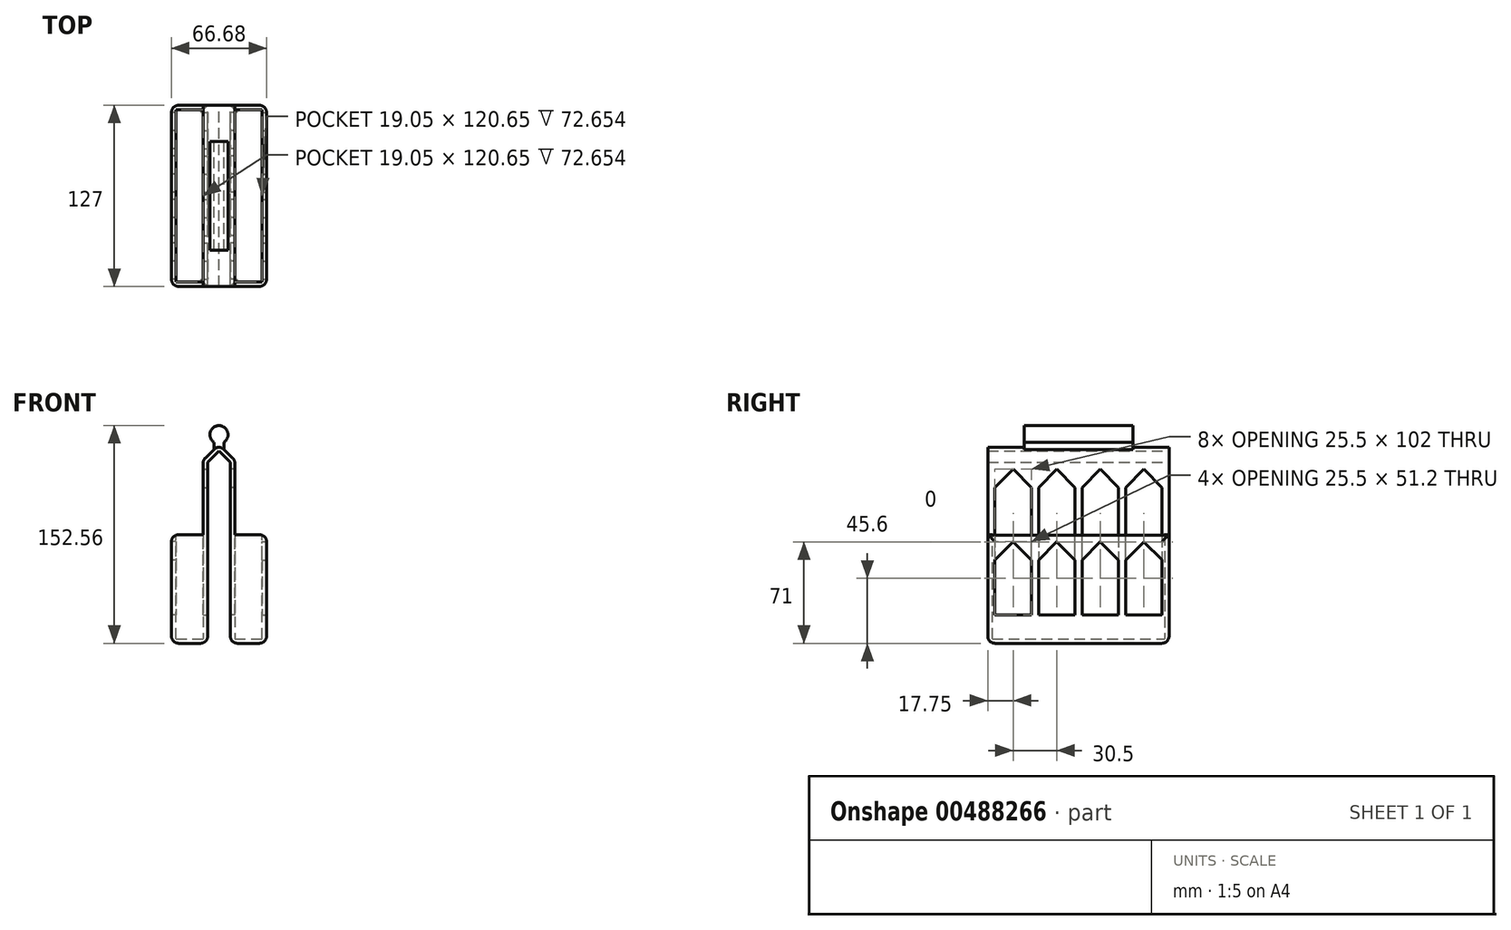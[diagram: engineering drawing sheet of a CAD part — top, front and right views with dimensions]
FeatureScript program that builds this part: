
annotation { "Feature Type Name" : "Feature", "Feature Type Description" : "" }
export const myFeature = defineFeature(function(context is Context, id is Id, definition is map)
    precondition{}
    {
        {
            var Q0;
            Q0=qCreatedBy(makeId("Front.planeOp"),FACE);
            var sketch = newSketch(context, id + "F0", { "sketchPlane" : qUnion([Q0])});
            skLineSegment(sketch, "E0.MirrorCS", {"start": v(7.94, 45.45) * mm, "end": v(0, 53.39) * mm});
            skLineSegment(sketch, "E1.MirrorCS", {"start": v(7.94, 45.45) * mm, "end": v(7.94, -81.55) * mm});
            skLineSegment(sketch, "E2.MirrorCS", {"start": v(7.94, -81.55) * mm, "end": v(33.34, -81.55) * mm});
            skLineSegment(sketch, "E3.MirrorCS", {"start": v(33.34, -81.55) * mm, "end": v(33.34, -5.35) * mm});
            skLineSegment(sketch, "E4.4", {"start": v(30.16, -78.37) * mm, "end": v(30.16, -5.35) * mm});
            skLineSegment(sketch, "E4.5", {"start": v(11.11, -78.37) * mm, "end": v(30.16, -78.37) * mm});
            skLineSegment(sketch, "E4.6", {"start": v(11.11, 46.77) * mm, "end": v(11.11, -78.37) * mm});
            skLineSegment(sketch, "E4.7", {"start": v(11.11, 46.77) * mm, "end": v(0, 57.88) * mm});
            skLineSegment(sketch, "E5", {"start": v(30.16, -5.35) * mm, "end": v(33.34, -5.35) * mm});
            skLineSegment(sketch, "E6", {"start": v(0, 57.88) * mm, "end": v(0, 53.39) * mm});
            skSolve(sketch);
        }
        {
            var Q0;
            Q0=makeQuery(id+"F0.imprint","IMPRINT",FACE,{"disambiguationData":[TD([[makeQuery(id+"F0.imprint","IMPRINT",EDGE,{"derivedFrom":sQuery(id+"F0.wireOp",EDGE,"E0.MirrorCS")}),-1.0]])]});
            extrude(context, id + "F1", {"entities" : qUnion([Q0]), "depth" : 127 * mm, "symmetric" : true});
        }
        {
            var Q0;
            Q0=makeQuery(id+"F1.opExtrude","SWEPT_FACE",FACE,{"disambiguationData":[OSD([sQuery(id+"F0.wireOp",EDGE,"E3.MirrorCS")])]});
            var sketch = newSketch(context, id + "F2", { "sketchPlane" : qUnion([Q0])});
            skLineSegment(sketch, "E7", {"start": v(-58.5, -23.1) * mm, "end": v(-58.5, -61.55) * mm});
            skLineSegment(sketch, "E8", {"start": v(-58.5, -61.55) * mm, "end": v(-33, -61.55) * mm});
            skLineSegment(sketch, "E9", {"start": v(-33, -61.55) * mm, "end": v(-33, -23.1) * mm});
            skLineSegment(sketch, "E10", {"start": v(-33, -23.1) * mm, "end": v(-45.75, -10.35) * mm});
            skLineSegment(sketch, "E11", {"start": v(-45.75, -10.35) * mm, "end": v(-58.5, -23.1) * mm});
            skLineSegment(sketch, "E12", {"start": v(-28, -61.55) * mm, "end": v(-2.5, -61.55) * mm});
            skLineSegment(sketch, "E13", {"start": v(-2.5, -61.55) * mm, "end": v(-2.5, -23.1) * mm});
            skLineSegment(sketch, "E14", {"start": v(-2.5, -23.1) * mm, "end": v(-15.25, -10.35) * mm});
            skLineSegment(sketch, "E15", {"start": v(-15.25, -10.35) * mm, "end": v(-28, -23.1) * mm});
            skLineSegment(sketch, "E16", {"start": v(-28, -23.1) * mm, "end": v(-28, -61.55) * mm});
            skLineSegment(sketch, "E17.MirrorCS", {"start": v(58.5, -61.55) * mm, "end": v(33, -61.55) * mm});
            skLineSegment(sketch, "E18.MirrorCS", {"start": v(45.75, -10.35) * mm, "end": v(58.5, -23.1) * mm});
            skLineSegment(sketch, "E19.MirrorCS", {"start": v(2.5, -61.55) * mm, "end": v(2.5, -23.1) * mm});
            skLineSegment(sketch, "E20.MirrorCS", {"start": v(28, -61.55) * mm, "end": v(2.5, -61.55) * mm});
            skLineSegment(sketch, "E21.MirrorCS", {"start": v(33, -61.55) * mm, "end": v(33, -23.1) * mm});
            skLineSegment(sketch, "E22.MirrorCS", {"start": v(15.25, -10.35) * mm, "end": v(28, -23.1) * mm});
            skLineSegment(sketch, "E23.MirrorCS", {"start": v(58.5, -23.1) * mm, "end": v(58.5, -61.55) * mm});
            skLineSegment(sketch, "E24.MirrorCS", {"start": v(28, -23.1) * mm, "end": v(28, -61.55) * mm});
            skLineSegment(sketch, "E25.MirrorCS", {"start": v(33, -23.1) * mm, "end": v(45.75, -10.35) * mm});
            skLineSegment(sketch, "E26.MirrorCS", {"start": v(2.5, -23.1) * mm, "end": v(15.25, -10.35) * mm});
            skSolve(sketch);
        }
        {
            var Q0;
            Q0=makeQuery(id+"F2.imprint","IMPRINT",FACE,{"disambiguationData":[TD([[makeQuery(id+"F2.imprint","IMPRINT",EDGE,{"derivedFrom":sQuery(id+"F2.wireOp",EDGE,"E7")}),1.0]])]});
            var Q1;
            Q1=makeQuery(id+"F2.imprint","IMPRINT",FACE,{"disambiguationData":[TD([[makeQuery(id+"F2.imprint","IMPRINT",EDGE,{"derivedFrom":sQuery(id+"F2.wireOp",EDGE,"E12")}),1.0]])]});
            var Q2;
            Q2=makeQuery(id+"F2.imprint","IMPRINT",FACE,{"disambiguationData":[TD([[makeQuery(id+"F2.imprint","IMPRINT",EDGE,{"derivedFrom":sQuery(id+"F2.wireOp",EDGE,"E19.MirrorCS")}),-1.0]])]});
            var Q3;
            Q3=makeQuery(id+"F2.imprint","IMPRINT",FACE,{"disambiguationData":[TD([[makeQuery(id+"F2.imprint","IMPRINT",EDGE,{"derivedFrom":sQuery(id+"F2.wireOp",EDGE,"E17.MirrorCS")}),-1.0]])]});
            extrude(context, id + "F3", {"entities" : qUnion([Q0, Q1, Q2, Q3]), "operationType" : NewBodyOperationType.REMOVE, "endBound" : BoundingType.UP_TO_NEXT, "oppositeDirection" : true, "depth" : 25.4 * mm});
        }
        {
            var Q0;
            Q0=makeQuery(id+"F1.opExtrude","SWEPT_FACE",FACE,{"disambiguationData":[OSD([sQuery(id+"F0.wireOp",EDGE,"E1.MirrorCS")])]});
            var sketch = newSketch(context, id + "F4", { "sketchPlane" : qUnion([Q0])});
            skLineSegment(sketch, "E27", {"start": v(-58.5, 27.7) * mm, "end": v(-58.5, -61.55) * mm});
            skLineSegment(sketch, "E28", {"start": v(-58.5, -61.55) * mm, "end": v(-33, -61.55) * mm});
            skLineSegment(sketch, "E29", {"start": v(-33, -61.55) * mm, "end": v(-33, 27.7) * mm});
            skLineSegment(sketch, "E30", {"start": v(-33, 27.7) * mm, "end": v(-45.75, 40.45) * mm});
            skLineSegment(sketch, "E31", {"start": v(-45.75, 40.45) * mm, "end": v(-58.5, 27.7) * mm});
            skLineSegment(sketch, "E32", {"start": v(-28, -61.55) * mm, "end": v(-2.5, -61.55) * mm});
            skLineSegment(sketch, "E33", {"start": v(-2.5, -61.55) * mm, "end": v(-2.5, 27.7) * mm});
            skLineSegment(sketch, "E34", {"start": v(-2.5, 27.7) * mm, "end": v(-15.25, 40.45) * mm});
            skLineSegment(sketch, "E35", {"start": v(-15.25, 40.45) * mm, "end": v(-28, 27.7) * mm});
            skLineSegment(sketch, "E36", {"start": v(-28, 27.7) * mm, "end": v(-28, -61.55) * mm});
            skLineSegment(sketch, "E37.MirrorCS", {"start": v(58.5, 27.7) * mm, "end": v(58.5, -61.55) * mm});
            skLineSegment(sketch, "E38.MirrorCS", {"start": v(58.5, -61.55) * mm, "end": v(33, -61.55) * mm});
            skLineSegment(sketch, "E39.MirrorCS", {"start": v(33, -61.55) * mm, "end": v(33, 27.7) * mm});
            skLineSegment(sketch, "E40.MirrorCS", {"start": v(33, 27.7) * mm, "end": v(45.75, 40.45) * mm});
            skLineSegment(sketch, "E41.MirrorCS", {"start": v(28, 27.7) * mm, "end": v(28, -61.55) * mm});
            skLineSegment(sketch, "E42.MirrorCS", {"start": v(45.75, 40.45) * mm, "end": v(58.5, 27.7) * mm});
            skLineSegment(sketch, "E43.MirrorCS", {"start": v(28, -61.55) * mm, "end": v(2.5, -61.55) * mm});
            skLineSegment(sketch, "E44.MirrorCS", {"start": v(15.25, 40.45) * mm, "end": v(28, 27.7) * mm});
            skLineSegment(sketch, "E45.MirrorCS", {"start": v(2.5, -61.55) * mm, "end": v(2.5, 27.7) * mm});
            skLineSegment(sketch, "E46.MirrorCS", {"start": v(2.5, 27.7) * mm, "end": v(15.25, 40.45) * mm});
            skSolve(sketch);
        }
        {
            var Q0;
            Q0=makeQuery(id+"F4.imprint","IMPRINT",FACE,{"disambiguationData":[TD([[makeQuery(id+"F4.imprint","IMPRINT",EDGE,{"derivedFrom":sQuery(id+"F4.wireOp",EDGE,"E27")}),1.0]])]});
            var Q1;
            Q1=makeQuery(id+"F4.imprint","IMPRINT",FACE,{"disambiguationData":[TD([[makeQuery(id+"F4.imprint","IMPRINT",EDGE,{"derivedFrom":sQuery(id+"F4.wireOp",EDGE,"E32")}),1.0]])]});
            var Q2;
            Q2=makeQuery(id+"F4.imprint","IMPRINT",FACE,{"disambiguationData":[TD([[makeQuery(id+"F4.imprint","IMPRINT",EDGE,{"derivedFrom":sQuery(id+"F4.wireOp",EDGE,"E41.MirrorCS")}),-1.0]])]});
            var Q3;
            Q3=makeQuery(id+"F4.imprint","IMPRINT",FACE,{"disambiguationData":[TD([[makeQuery(id+"F4.imprint","IMPRINT",EDGE,{"derivedFrom":sQuery(id+"F4.wireOp",EDGE,"E37.MirrorCS")}),-1.0]])]});
            extrude(context, id + "F5", {"entities" : qUnion([Q0, Q1, Q2, Q3]), "operationType" : NewBodyOperationType.REMOVE, "endBound" : BoundingType.UP_TO_NEXT, "oppositeDirection" : true, "depth" : 25.4 * mm});
        }
        {
            var Q0;
            Q0=makeQuery(id+"F1.opExtrude","SWEPT_BODY",BODY,{"disambiguationData":[OSD([sQuery(id+"F0.wireOp",EDGE,"E0.MirrorCS"),sQuery(id+"F0.wireOp",EDGE,"E1.MirrorCS"),sQuery(id+"F0.wireOp",EDGE,"E2.MirrorCS"),sQuery(id+"F0.wireOp",EDGE,"E3.MirrorCS"),sQuery(id+"F0.wireOp",EDGE,"E4.4"),sQuery(id+"F0.wireOp",EDGE,"E4.5"),sQuery(id+"F0.wireOp",EDGE,"E4.6"),sQuery(id+"F0.wireOp",EDGE,"E4.7"),sQuery(id+"F0.wireOp",EDGE,"E5"),sQuery(id+"F0.wireOp",EDGE,"E6")])]});
            var Q1;
            Q1=qCreatedBy(makeId("Right.planeOp"),FACE);
            mirror(context, id + "F6", {"operationType" : NewBodyOperationType.ADD, "entities" : qUnion([Q0]), "mirrorPlane" : qUnion([Q1])});
        }
        {
            var Q0;
            {var subQ0=makeQuery(id+"F1.opExtrude","CAP_FACE",FACE,{"disambiguationData":[OSD([sQuery(id+"F0.wireOp",EDGE,"E0.MirrorCS"),sQuery(id+"F0.wireOp",EDGE,"E1.MirrorCS"),sQuery(id+"F0.wireOp",EDGE,"E2.MirrorCS"),sQuery(id+"F0.wireOp",EDGE,"E3.MirrorCS"),sQuery(id+"F0.wireOp",EDGE,"E4.4"),sQuery(id+"F0.wireOp",EDGE,"E4.5"),sQuery(id+"F0.wireOp",EDGE,"E4.6"),sQuery(id+"F0.wireOp",EDGE,"E4.7"),sQuery(id+"F0.wireOp",EDGE,"E5"),sQuery(id+"F0.wireOp",EDGE,"E6")])],"isStart":true});Q0=makeQuery(id+"F6.boolean.opBoolean","MERGE",FACE,{"derivedFrom":[subQ0,makeQuery(id+"F6.opPattern","COPY",FACE,{"derivedFrom":subQ0,"instanceName":"1"})]});}
            var sketch = newSketch(context, id + "F7", { "sketchPlane" : qUnion([Q0])});
            skLineSegment(sketch, "E47.bottom", {"start": v(-33.34, -5.35) * mm, "end": v(-7.94, -5.35) * mm});
            skLineSegment(sketch, "E47.top", {"start": v(-33.34, -81.55) * mm, "end": v(-7.94, -81.55) * mm});
            skLineSegment(sketch, "E47.left", {"start": v(-33.34, -5.35) * mm, "end": v(-33.34, -81.55) * mm});
            skLineSegment(sketch, "E47.right", {"start": v(-7.94, -5.35) * mm, "end": v(-7.94, -81.55) * mm});
            skLineSegment(sketch, "E48.bottom", {"start": v(33.34, -5.35) * mm, "end": v(7.94, -5.35) * mm});
            skLineSegment(sketch, "E48.top", {"start": v(33.34, -81.55) * mm, "end": v(7.94, -81.55) * mm});
            skLineSegment(sketch, "E48.left", {"start": v(33.34, -5.35) * mm, "end": v(33.34, -81.55) * mm});
            skLineSegment(sketch, "E48.right", {"start": v(7.94, -5.35) * mm, "end": v(7.94, -81.55) * mm});
            skSolve(sketch);
        }
        {
            var Q0;
            {var subQ1=makeQuery(id+"F1.opExtrude","CAP_EDGE",EDGE,{"disambiguationData":[OSD([sQuery(id+"F0.wireOp",EDGE,"E4.4")])],"isStart":true});Q0=makeQuery(id+"F7.imprint","IMPRINT",FACE,{"disambiguationData":[TD([[makeQuery(id+"F7.imprint","IMPRINT",EDGE,{"derivedFrom":subQ1}),-1.0]])]});}
            var Q1;
            Q1=makeQuery(id+"F7.imprint","IMPRINT",FACE,{"disambiguationData":[TD([[makeQuery(id+"F7.imprint","IMPRINT",EDGE,{"derivedFrom":sQuery(id+"F7.wireOp",EDGE,"E47.top")}),-1.0]])]});
            var Q2;
            {var subQ1=makeQuery(id+"F6.opPattern","COPY",EDGE,{"derivedFrom":makeQuery(id+"F1.opExtrude","CAP_EDGE",EDGE,{"disambiguationData":[OSD([sQuery(id+"F0.wireOp",EDGE,"E4.4")])],"isStart":true}),"instanceName":"1"});Q2=makeQuery(id+"F7.imprint","IMPRINT",FACE,{"disambiguationData":[TD([[makeQuery(id+"F7.imprint","IMPRINT",EDGE,{"derivedFrom":subQ1}),1.0]])]});}
            var Q3;
            Q3=makeQuery(id+"F7.imprint","IMPRINT",FACE,{"disambiguationData":[TD([[makeQuery(id+"F7.imprint","IMPRINT",EDGE,{"derivedFrom":sQuery(id+"F7.wireOp",EDGE,"E48.top")}),1.0]])]});
            extrude(context, id + "F8", {"entities" : qUnion([Q0, Q1, Q2, Q3]), "operationType" : NewBodyOperationType.ADD, "oppositeDirection" : true, "depth" : 3.17 * mm});
        }
        {
            var Q0;
            {var subQ0=makeQuery(id+"F1.opExtrude","CAP_FACE",FACE,{"disambiguationData":[OSD([sQuery(id+"F0.wireOp",EDGE,"E0.MirrorCS"),sQuery(id+"F0.wireOp",EDGE,"E1.MirrorCS"),sQuery(id+"F0.wireOp",EDGE,"E2.MirrorCS"),sQuery(id+"F0.wireOp",EDGE,"E3.MirrorCS"),sQuery(id+"F0.wireOp",EDGE,"E4.4"),sQuery(id+"F0.wireOp",EDGE,"E4.5"),sQuery(id+"F0.wireOp",EDGE,"E4.6"),sQuery(id+"F0.wireOp",EDGE,"E4.7"),sQuery(id+"F0.wireOp",EDGE,"E5"),sQuery(id+"F0.wireOp",EDGE,"E6")])],"isStart":false});Q0=makeQuery(id+"F6.boolean.opBoolean","MERGE",FACE,{"derivedFrom":[subQ0,makeQuery(id+"F6.opPattern","COPY",FACE,{"derivedFrom":subQ0,"instanceName":"1"})]});}
            var sketch = newSketch(context, id + "F9", { "sketchPlane" : qUnion([Q0])});
            skLineSegment(sketch, "E49.bottom", {"start": v(-33.34, -5.35) * mm, "end": v(-7.94, -5.35) * mm});
            skLineSegment(sketch, "E49.top", {"start": v(-33.34, -81.55) * mm, "end": v(-7.94, -81.55) * mm});
            skLineSegment(sketch, "E49.left", {"start": v(-33.34, -5.35) * mm, "end": v(-33.34, -81.55) * mm});
            skLineSegment(sketch, "E49.right", {"start": v(-7.94, -5.35) * mm, "end": v(-7.94, -81.55) * mm});
            skLineSegment(sketch, "E50.bottom", {"start": v(33.34, -5.35) * mm, "end": v(7.94, -5.35) * mm});
            skLineSegment(sketch, "E50.top", {"start": v(33.34, -81.55) * mm, "end": v(7.94, -81.55) * mm});
            skLineSegment(sketch, "E50.left", {"start": v(33.34, -5.35) * mm, "end": v(33.34, -81.55) * mm});
            skLineSegment(sketch, "E50.right", {"start": v(7.94, -5.35) * mm, "end": v(7.94, -81.55) * mm});
            skSolve(sketch);
        }
        {
            var Q0;
            {var subQ1=makeQuery(id+"F6.opPattern","COPY",EDGE,{"derivedFrom":makeQuery(id+"F1.opExtrude","CAP_EDGE",EDGE,{"disambiguationData":[OSD([sQuery(id+"F0.wireOp",EDGE,"E4.4")])],"isStart":false}),"instanceName":"1"});Q0=makeQuery(id+"F9.imprint","IMPRINT",FACE,{"disambiguationData":[TD([[makeQuery(id+"F9.imprint","IMPRINT",EDGE,{"derivedFrom":subQ1}),-1.0]])]});}
            var Q1;
            Q1=makeQuery(id+"F9.imprint","IMPRINT",FACE,{"disambiguationData":[TD([[makeQuery(id+"F9.imprint","IMPRINT",EDGE,{"derivedFrom":sQuery(id+"F9.wireOp",EDGE,"E49.top")}),-1.0]])]});
            var Q2;
            Q2=makeQuery(id+"F9.imprint","IMPRINT",FACE,{"disambiguationData":[TD([[makeQuery(id+"F9.imprint","IMPRINT",EDGE,{"derivedFrom":sQuery(id+"F9.wireOp",EDGE,"E50.top")}),1.0]])]});
            var Q3;
            {var subQ1=makeQuery(id+"F1.opExtrude","CAP_EDGE",EDGE,{"disambiguationData":[OSD([sQuery(id+"F0.wireOp",EDGE,"E4.4")])],"isStart":false});Q3=makeQuery(id+"F9.imprint","IMPRINT",FACE,{"disambiguationData":[TD([[makeQuery(id+"F9.imprint","IMPRINT",EDGE,{"derivedFrom":subQ1}),1.0]])]});}
            extrude(context, id + "F10", {"entities" : qUnion([Q0, Q1, Q2, Q3]), "operationType" : NewBodyOperationType.ADD, "oppositeDirection" : true, "depth" : 3.17 * mm});
        }
        {
            var Q0;
            {var subQ0=sQuery(id+"F0.wireOp",EDGE,"E4.7");var subQ2=makeQuery(id+"F1.opExtrude","SWEPT_EDGE",EDGE,{"disambiguationData":[OSD([subQ0,sQuery(id+"F0.wireOp",EDGE,"E6")])]});Q0=makeQuery(id+"FHTwIT9TmEUB8w3_1.boolean.opBoolean","SPLIT",EDGE,{"disambiguationData":[TD([makeQuery(id+"FHTwIT9TmEUB8w3_1.opExtrude","SWEPT_FACE",FACE,{"disambiguationData":[OSD([sQuery(id+"FMn76epO6iGozmc_1.wireOp",EDGE,"xZxAHIdV-4ATv-dNtP-2BFV-Ot14Agv0DBSX.left")])]})])],"derivedFrom":makeQuery(id+"F6.boolean.opBoolean","MERGE",EDGE,{"derivedFrom":[subQ2,makeQuery(id+"F6.opPattern","COPY",EDGE,{"derivedFrom":subQ2,"instanceName":"1"})]})});}
            var Q1;
            {var subQ0=sQuery(id+"F0.wireOp",EDGE,"E6");var subQ1=sQuery(id+"F0.wireOp",EDGE,"E4.7");var subQ4=makeQuery(id+"F1.opExtrude","SWEPT_EDGE",EDGE,{"disambiguationData":[OSD([subQ1,subQ0])]});Q1=makeQuery(id+"FHTwIT9TmEUB8w3_1.boolean.opBoolean","SPLIT",EDGE,{"disambiguationData":[TD([makeQuery(id+"FHTwIT9TmEUB8w3_1.opExtrude","SWEPT_FACE",FACE,{"disambiguationData":[OSD([sQuery(id+"FMn76epO6iGozmc_1.wireOp",EDGE,"d1a49dbe-07ff-4782-87ab-37d6159794840.MirrorCS")])]})])],"derivedFrom":makeQuery(id+"F6.boolean.opBoolean","MERGE",EDGE,{"derivedFrom":[subQ4,makeQuery(id+"F6.opPattern","COPY",EDGE,{"derivedFrom":subQ4,"instanceName":"1"})]})});}
            var Q2;
            {var subQ0=sQuery(id+"F0.wireOp",EDGE,"E6");var subQ1=sQuery(id+"F0.wireOp",EDGE,"E4.7");var subQ4=makeQuery(id+"F1.opExtrude","SWEPT_EDGE",EDGE,{"disambiguationData":[OSD([subQ1,subQ0])]});Q2=makeQuery(id+"FHTwIT9TmEUB8w3_1.boolean.opBoolean","SPLIT",EDGE,{"disambiguationData":[TD([makeQuery(id+"FHTwIT9TmEUB8w3_1.opExtrude","SWEPT_FACE",FACE,{"disambiguationData":[OSD([sQuery(id+"FMn76epO6iGozmc_1.wireOp",EDGE,"lcgLJjxl-wOVu-M8rO-XfpG-uKA0rGEyVEIE.left")])]})])],"derivedFrom":makeQuery(id+"F6.boolean.opBoolean","MERGE",EDGE,{"derivedFrom":[subQ4,makeQuery(id+"F6.opPattern","COPY",EDGE,{"derivedFrom":subQ4,"instanceName":"1"})]})});}
            var Q3;
            Q3=makeQuery(id+"F6.opPattern","COPY",EDGE,{"derivedFrom":makeQuery(id+"F1.opExtrude","SWEPT_EDGE",EDGE,{"disambiguationData":[OSD([sQuery(id+"F0.wireOp",EDGE,"E4.6"),sQuery(id+"F0.wireOp",EDGE,"E4.7")])]}),"instanceName":"1"});
            var Q4;
            Q4=makeQuery(id+"F1.opExtrude","SWEPT_EDGE",EDGE,{"disambiguationData":[OSD([sQuery(id+"F0.wireOp",EDGE,"E4.6"),sQuery(id+"F0.wireOp",EDGE,"E4.7")])]});
            fillet(context, id + "F11", {"entities" : qUnion([Q0, Q1, Q2, Q3, Q4]), "radius" : 5.08 * mm, "tangentPropagation" : true, "allowEdgeOverflow" : false});
        }
        {
            var Q0;
            Q0=makeQuery(id+"F6.opPattern","COPY",EDGE,{"derivedFrom":makeQuery(id+"F1.opExtrude","CAP_EDGE",EDGE,{"disambiguationData":[OSD([sQuery(id+"F0.wireOp",EDGE,"E2.MirrorCS")])],"isStart":false}),"instanceName":"1"});
            var Q1;
            Q1=makeQuery(id+"F6.opPattern","COPY",EDGE,{"derivedFrom":makeQuery(id+"F1.opExtrude","SWEPT_EDGE",EDGE,{"disambiguationData":[OSD([sQuery(id+"F0.wireOp",EDGE,"E2.MirrorCS"),sQuery(id+"F0.wireOp",EDGE,"E3.MirrorCS")])]}),"instanceName":"1"});
            var Q2;
            Q2=makeQuery(id+"F6.opPattern","COPY",EDGE,{"derivedFrom":makeQuery(id+"F1.opExtrude","CAP_EDGE",EDGE,{"disambiguationData":[OSD([sQuery(id+"F0.wireOp",EDGE,"E2.MirrorCS")])],"isStart":true}),"instanceName":"1"});
            var Q3;
            Q3=makeQuery(id+"F6.opPattern","COPY",EDGE,{"derivedFrom":makeQuery(id+"F1.opExtrude","SWEPT_EDGE",EDGE,{"disambiguationData":[OSD([sQuery(id+"F0.wireOp",EDGE,"E1.MirrorCS"),sQuery(id+"F0.wireOp",EDGE,"E2.MirrorCS")])]}),"instanceName":"1"});
            var Q4;
            Q4=makeQuery(id+"F1.opExtrude","SWEPT_EDGE",EDGE,{"disambiguationData":[OSD([sQuery(id+"F0.wireOp",EDGE,"E1.MirrorCS"),sQuery(id+"F0.wireOp",EDGE,"E2.MirrorCS")])]});
            var Q5;
            Q5=makeQuery(id+"F1.opExtrude","CAP_EDGE",EDGE,{"disambiguationData":[OSD([sQuery(id+"F0.wireOp",EDGE,"E2.MirrorCS")])],"isStart":false});
            var Q6;
            Q6=makeQuery(id+"F1.opExtrude","SWEPT_FACE",FACE,{"disambiguationData":[OSD([sQuery(id+"F0.wireOp",EDGE,"E2.MirrorCS")])]});
            var Q7;
            Q7=makeQuery(id+"F1.opExtrude","SWEPT_EDGE",EDGE,{"disambiguationData":[OSD([sQuery(id+"F0.wireOp",EDGE,"E3.MirrorCS"),sQuery(id+"F0.wireOp",EDGE,"E5")])]});
            var Q8;
            Q8=makeQuery(id+"F6.opPattern","COPY",EDGE,{"derivedFrom":makeQuery(id+"F1.opExtrude","SWEPT_EDGE",EDGE,{"disambiguationData":[OSD([sQuery(id+"F0.wireOp",EDGE,"E3.MirrorCS"),sQuery(id+"F0.wireOp",EDGE,"E5")])]}),"instanceName":"1"});
            var Q9;
            Q9=makeQuery(id+"F6.opPattern","COPY",EDGE,{"derivedFrom":makeQuery(id+"F1.opExtrude","CAP_EDGE",EDGE,{"disambiguationData":[OSD([sQuery(id+"F0.wireOp",EDGE,"E3.MirrorCS")])],"isStart":false}),"instanceName":"1"});
            var Q10;
            Q10=makeQuery(id+"F6.opPattern","COPY",EDGE,{"derivedFrom":makeQuery(id+"F1.opExtrude","CAP_EDGE",EDGE,{"disambiguationData":[OSD([sQuery(id+"F0.wireOp",EDGE,"E3.MirrorCS")])],"isStart":true}),"instanceName":"1"});
            var Q11;
            Q11=makeQuery(id+"F1.opExtrude","CAP_EDGE",EDGE,{"disambiguationData":[OSD([sQuery(id+"F0.wireOp",EDGE,"E3.MirrorCS")])],"isStart":true});
            var Q12;
            Q12=makeQuery(id+"F1.opExtrude","CAP_EDGE",EDGE,{"disambiguationData":[OSD([sQuery(id+"F0.wireOp",EDGE,"E3.MirrorCS")])],"isStart":false});
            fillet(context, id + "F12", {"entities" : qUnion([Q0, Q1, Q2, Q3, Q4, Q5, Q6, Q7, Q8, Q9, Q10, Q11, Q12]), "radius" : 5.08 * mm, "tangentPropagation" : true, "allowEdgeOverflow" : false});
        }
        {
            var Q0;
            Q0=qCreatedBy(makeId("Front.planeOp"),FACE);
            var sketch = newSketch(context, id + "F13", { "sketchPlane" : qUnion([Q0])});
            skCircle(sketch, "E51", {"center": v(0, 64.66) * mm, "radius": 6.35 * mm});
            skArc(sketch, "E52.0", {"start": v(3.6, 54.29) * mm, "mid": v(0, 55.77) * mm, "end": v(-3.6, 54.29) * mm});
            skPoint(sketch, "E52.1", {"position": v(0, 55.77) * mm});
            skLineSegment(sketch, "E53", {"start": v(-3.6, 54.29) * mm, "end": v(-3.6, 59.43) * mm});
            skLineSegment(sketch, "E54", {"start": v(3.6, 54.29) * mm, "end": v(3.6, 59.43) * mm});
            skSolve(sketch);
        }
        {
            var Q0;
            {var subQ0=sQuery(id+"F13.wireOp",EDGE,"E51");var subQ1=makeQuery(id+"F13.imprint","INTERSECT",VERTEX,{"derivedFrom":[subQ0,sQuery(id+"F13.wireOp",EDGE,"E53")]});Q0=makeQuery(id+"F13.imprint","IMPRINT",FACE,{"disambiguationData":[TD([[makeQuery(id+"F13.imprint","IMPRINT",EDGE,{"disambiguationData":[TD([[subQ1,-1.0]])],"derivedFrom":subQ0}),1.0]])]});}
            var Q1;
            Q1=makeQuery(id+"F13.imprint","IMPRINT",FACE,{"disambiguationData":[TD([[makeQuery(id+"F13.imprint","IMPRINT",EDGE,{"derivedFrom":sQuery(id+"F13.wireOp",EDGE,"E52.0")}),-1.0]])]});
            extrude(context, id + "F14", {"entities" : qUnion([Q0, Q1]), "operationType" : NewBodyOperationType.ADD, "depth" : 76.2 * mm, "symmetric" : true});
        }
    });
